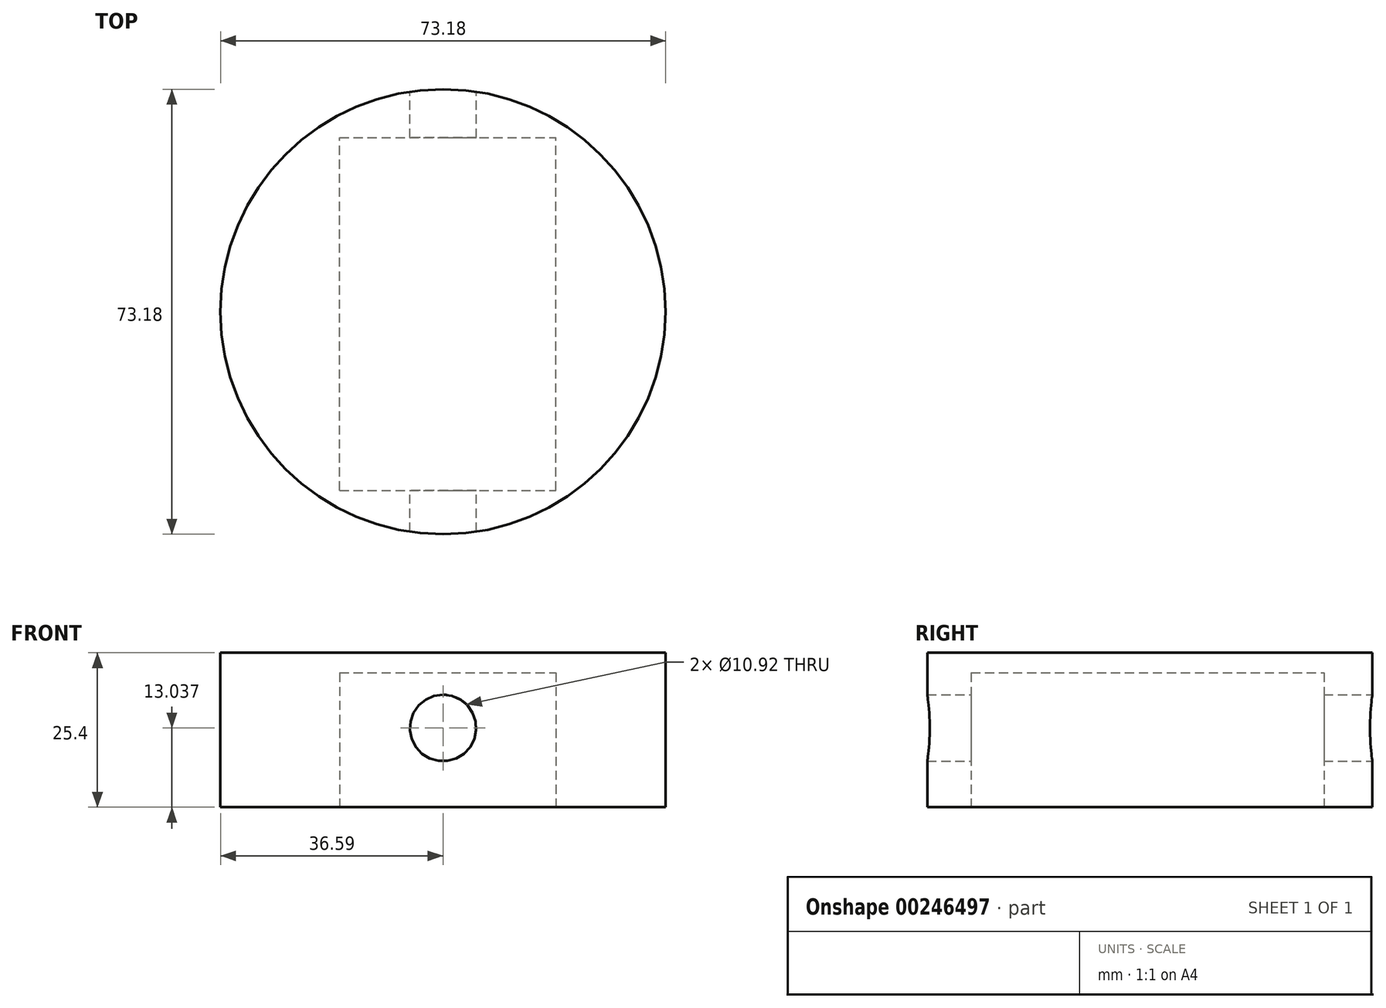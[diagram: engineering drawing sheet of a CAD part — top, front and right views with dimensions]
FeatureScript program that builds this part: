
annotation { "Feature Type Name" : "Feature", "Feature Type Description" : "" }
export const myFeature = defineFeature(function(context is Context, id is Id, definition is map)
    precondition{}
    {
        {
            var Q0;
            Q0=qCreatedBy(makeId("Top.planeOp"),FACE);
            var sketch = newSketch(context, id + "F0", { "sketchPlane" : qUnion([Q0])});
            skCircle(sketch, "E0", {"center": v(0, 0) * mm, "radius": 36.6 * mm});
            skSolve(sketch);
        }
        {
            var Q0;
            Q0=makeQuery(id+"F0.imprint","IMPRINT",FACE,{"disambiguationData":[TD([[makeQuery(id+"F0.imprint","IMPRINT",EDGE,{"derivedFrom":sQuery(id+"F0.wireOp",EDGE,"E0")}),1.0]])]});
            extrude(context, id + "F1", {"entities" : qUnion([Q0]), "depth" : 25.4 * mm});
        }
        {
            var Q0;
            Q0=qCreatedBy(makeId("Front.planeOp"),FACE);
            cPlane(context, id + "F2", {"entities" : qUnion([Q0]), "cplaneType" : CPlaneType.OFFSET, "offset" : 37.08 * mm, "oppositeDirection" : true, "width" : 152.4 * mm, "height" : 152.4 * mm});
        }
        {
            var Q0;
            Q0=qCreatedBy(id+"F2.planeOp",FACE);
            var sketch = newSketch(context, id + "F3", { "sketchPlane" : qUnion([Q0])});
            skCircle(sketch, "E1", {"center": v(0, 13.04) * mm, "radius": 5.46 * mm});
            skSolve(sketch);
        }
        {
            var Q0;
            Q0 = qSketchRegion(id + "F3", true);
            extrude(context, id + "F4", {"entities" : qUnion([Q0]), "operationType" : NewBodyOperationType.REMOVE, "depth" : 76.7 * mm});
        }
        {
            var Q0;
            Q0=qCreatedBy(makeId("Top.planeOp"),FACE);
            var sketch = newSketch(context, id + "F5", { "sketchPlane" : qUnion([Q0])});
            skLineSegment(sketch, "E2.bottom", {"start": v(-17, -29.4) * mm, "end": v(18.53, -29.4) * mm});
            skLineSegment(sketch, "E2.top", {"start": v(-17, 28.63) * mm, "end": v(18.53, 28.63) * mm});
            skLineSegment(sketch, "E2.left", {"start": v(-17, -29.4) * mm, "end": v(-17, 28.63) * mm});
            skLineSegment(sketch, "E2.right", {"start": v(18.53, -29.4) * mm, "end": v(18.53, 28.63) * mm});
            skSolve(sketch);
        }
        {
            var Q0;
            Q0 = qSketchRegion(id + "F5", true);
            extrude(context, id + "F6", {"entities" : qUnion([Q0]), "operationType" : NewBodyOperationType.REMOVE, "depth" : 22.1 * mm});
        }
    });
